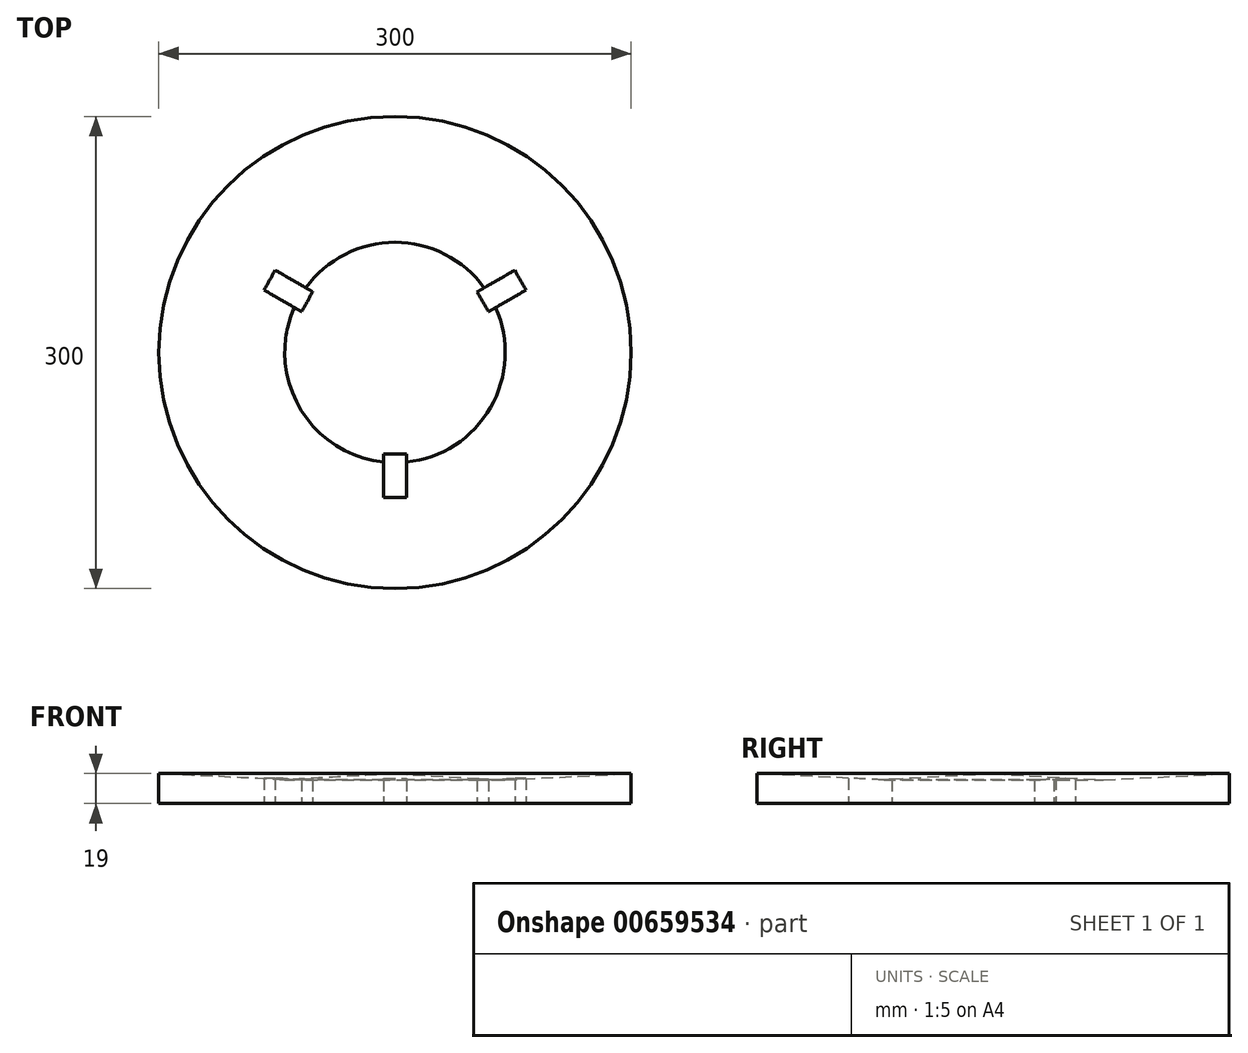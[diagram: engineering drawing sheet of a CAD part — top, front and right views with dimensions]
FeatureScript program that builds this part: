
annotation { "Feature Type Name" : "Feature", "Feature Type Description" : "" }
export const myFeature = defineFeature(function(context is Context, id is Id, definition is map)
    precondition{}
    {
        {
            var Q0;
            Q0=qCreatedBy(makeId("Front.planeOp"),FACE);
            var sketch = newSketch(context, id + "F0", { "sketchPlane" : qUnion([Q0])});
            skLineSegment(sketch, "E0", {"start": v(0, 0) * mm, "end": v(-150, 0) * mm});
            skLineSegment(sketch, "E1", {"start": v(-150, 0) * mm, "end": v(-150, 19) * mm});
            skLineSegment(sketch, "E2", {"start": v(0, 0) * mm, "end": v(-70, 0) * mm});
            skLineSegment(sketch, "E3", {"start": v(-70, 0) * mm, "end": v(-70, 15) * mm});
            skLineSegment(sketch, "E4", {"start": v(-70, 15) * mm, "end": v(-150, 19) * mm});
            skLineSegment(sketch, "E5", {"start": v(0, 0) * mm, "end": v(0, 19) * mm});
            skLineSegment(sketch, "E6", {"start": v(0, 19) * mm, "end": v(-70, 15) * mm});
            skLineSegment(sketch, "E7.MirrorCS", {"start": v(0, 0) * mm, "end": v(150, 0) * mm});
            skLineSegment(sketch, "E8.MirrorCS", {"start": v(0, 0) * mm, "end": v(70, 0) * mm});
            skLineSegment(sketch, "E9.MirrorCS", {"start": v(70, 0) * mm, "end": v(70, 15) * mm});
            skLineSegment(sketch, "E10.MirrorCS", {"start": v(70, 15) * mm, "end": v(150, 19) * mm});
            skLineSegment(sketch, "E11.MirrorCS", {"start": v(150, 0) * mm, "end": v(150, 19) * mm});
            skLineSegment(sketch, "E12.MirrorCS", {"start": v(0, 19) * mm, "end": v(70, 15) * mm});
            skSolve(sketch);
        }
        {
            var Q0;
            Q0=makeQuery(id+"F0.imprint","IMPRINT",FACE,{"disambiguationData":[TD([[makeQuery(id+"F0.imprint","IMPRINT",EDGE,{"derivedFrom":sQuery(id+"F0.wireOp",EDGE,"E0")}),-1.0]])]});
            var Q1;
            Q1=makeQuery(id+"F0.imprint","IMPRINT",FACE,{"disambiguationData":[TD([[makeQuery(id+"F0.imprint","IMPRINT",EDGE,{"derivedFrom":sQuery(id+"F0.wireOp",EDGE,"E2")}),-1.0]])]});
            var Q2;
            Q2=sQuery(id+"F0.wireOp",EDGE,"E5");
            revolve(context, id + "F1", {"entities" : qUnion([Q0, Q1]), "axis" : qUnion([Q2]), "revolveType" : RevolveType.FULL});
        }
        {
            var Q0;
            Q0=makeQuery(id+"F1.opRevolve","SWEPT_FACE",FACE,{"disambiguationData":[OSD([sQuery(id+"F0.wireOp",EDGE,"E0"),sQuery(id+"F0.wireOp",EDGE,"E2")])]});
            var sketch = newSketch(context, id + "F2", { "sketchPlane" : qUnion([Q0])});
            skLineSegment(sketch, "E13.bottom", {"start": v(7.25, 92) * mm, "end": v(-7.25, 92) * mm});
            skLineSegment(sketch, "E13.top", {"start": v(7.25, 64.5) * mm, "end": v(-7.25, 64.5) * mm});
            skLineSegment(sketch, "E13.left", {"start": v(7.25, 92) * mm, "end": v(7.25, 64.5) * mm});
            skLineSegment(sketch, "E13.right", {"start": v(-7.25, 92) * mm, "end": v(-7.25, 64.5) * mm});
            skPoint(sketch, "E13.middle", {"position": v(0, 78.25) * mm});
            skLineSegment(sketch, "E14.1.0", {"start": v(-59.48, -25.97) * mm, "end": v(-52.23, -38.53) * mm});
            skLineSegment(sketch, "E14.1.1", {"start": v(-76.05, -52.28) * mm, "end": v(-52.23, -38.53) * mm});
            skLineSegment(sketch, "E14.1.2", {"start": v(-83.3, -39.72) * mm, "end": v(-59.48, -25.97) * mm});
            skLineSegment(sketch, "E14.1.3", {"start": v(-83.3, -39.72) * mm, "end": v(-76.05, -52.28) * mm});
            skLineSegment(sketch, "E14.2.0", {"start": v(52.23, -38.53) * mm, "end": v(59.48, -25.97) * mm});
            skLineSegment(sketch, "E14.2.1", {"start": v(83.3, -39.72) * mm, "end": v(59.48, -25.97) * mm});
            skLineSegment(sketch, "E14.2.2", {"start": v(76.05, -52.28) * mm, "end": v(52.23, -38.53) * mm});
            skLineSegment(sketch, "E14.2.3", {"start": v(76.05, -52.28) * mm, "end": v(83.3, -39.72) * mm});
            skPoint(sketch, "E14.center", {"position": v(0, 0) * mm});
            skSolve(sketch);
        }
        {
            var Q0;
            Q0 = qSketchRegion(id + "F2", true);
            extrude(context, id + "F3", {"entities" : qUnion([Q0]), "operationType" : NewBodyOperationType.REMOVE, "endBound" : BoundingType.UP_TO_NEXT, "oppositeDirection" : true, "depth" : 25 * mm, "offsetDistance" : 25 * mm});
        }
    });
